# Revit family: Air_Gap-Zurn_Wilikns_Model_AG_12
name_source: partatom
category: Pipe Accessories
units: mm (PartAtom-declared; Revit-internal decimal feet)

## family parameters
Always vertical = Yes
Cut with Voids When Loaded = No
OmniClass Number = 23.65.55.14
OmniClass Title = Valves for Liquid Services
Part Type = Valve - Breaks Into
Round Connector Dimension = Use Radius
Shared = No
Work Plane-Based = No

## types (1)
- AG-12 (1 1/4"-2" 375 & 375XL Air Gap)
    Arm Edge = 0' - 0 3/8"
    Arm Large Thickness = 0' - 0 13/32"
    Arm Thickness = 0' - 0 3/16"
    Arm mid Distance = 0' - 6 11/32"
    Arm outer = 0' - 1 21/32"
    Arm width = 0' - 1"
    Assembly Code = D2020300
    Bolt Pitch = 0' - 2 1/2"
    Bolt circle from End = 0' - 0 1/4"
    Bolt hole = 0' - 0 3/16"
    Bolt hole Bush = 0' - 0 13/32"
    Center to Bolt Center = 0' - 1 11/16"
    DIM A WIDTH = 0' - 6 1/2"
    DIM B TOTAL LENGTH = 0' - 8"
    DIM C INNER DIAMETER = 0' - 3"
    Default Elevation = 0' - 0"
    Description = Air Gap Adaptor Fitting
    End Connection Width = 0' - 3 1/2"
    Flow Rate (GPM) = 0 GPM
    Height = 1' - 0"
    Length = 2' - 0"
    Main Material = Paint - Zurn - Cast Iron - Gray
    Manufacturer = Zurn Water, LLC
    Manufacturer Brand = Zurn Wilkins
    Max Working Water Pressure = 0.00 psi
    Max Working Water Temperature = 0 °F
    Model = AG-12
    Modified Date = 07/08/2025
    Nominal Diameter = 0' - 3"
    Nominal Radius = 0' - 1 1/2"
    OUTER RADIUS = 0' - 1 29/32"
    PIPE WIDTH = 0' - 1"
    Product Documentation Link = https://files.zurn.com
    Product Page URL = https://www.zurn.com
    Product Weight (lbs) = 1
    Product data URL = https://bimobject.com
    URL = www.zurn.com/

## geometry (parser evidence)
native form markers: Sweep x2
no freeform markers — native parametric forms only
